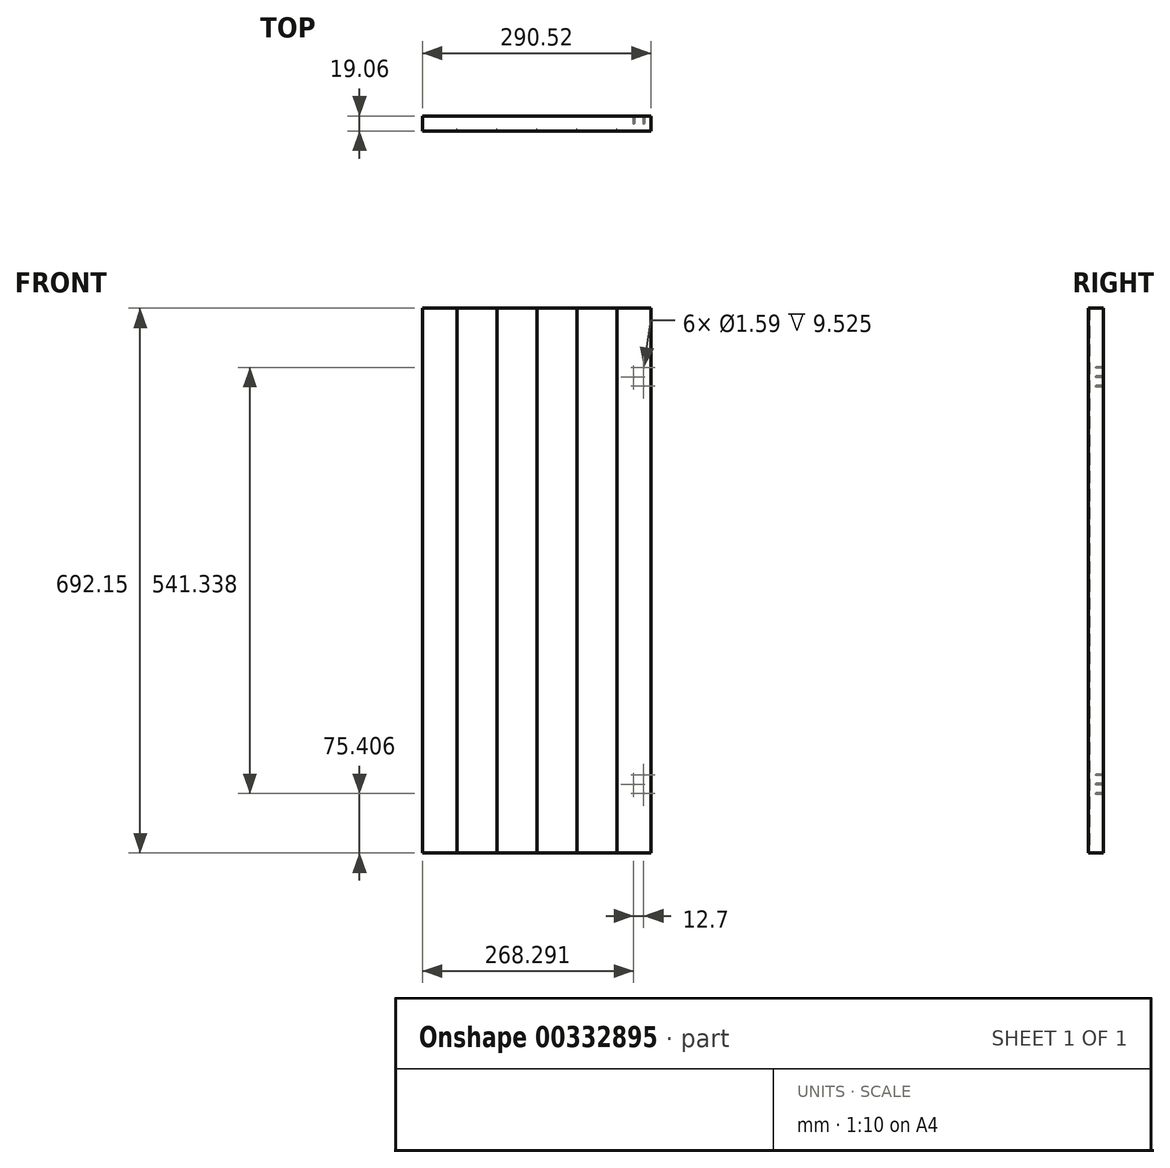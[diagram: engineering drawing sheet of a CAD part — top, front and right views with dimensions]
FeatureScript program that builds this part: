
annotation { "Feature Type Name" : "Feature", "Feature Type Description" : "" }
export const myFeature = defineFeature(function(context is Context, id is Id, definition is map)
    precondition{}
    {
        {
            var Q0;
            Q0=qCreatedBy(makeId("Top.planeOp"),FACE);
            var sketch = newSketch(context, id + "F0", { "sketchPlane" : qUnion([Q0])});
            skLineSegment(sketch, "E0.bottom", {"start": v(508, -9.53) * mm, "end": v(458.22, -9.53) * mm});
            skLineSegment(sketch, "E0.top", {"start": v(508, 9.53) * mm, "end": v(-508, 9.53) * mm});
            skLineSegment(sketch, "E0.left", {"start": v(508, 9.53) * mm, "end": v(508, -9.53) * mm});
            skLineSegment(sketch, "E0.right", {"start": v(-508, 9.53) * mm, "end": v(-508, -9.53) * mm});
            skPoint(sketch, "E0.middle", {"position": v(0, 0) * mm});
            skArc(sketch, "E1", {"start": v(-509.02, -9.53) * mm, "mid": v(-508.3, -9.23) * mm, "end": v(-508, -8.5) * mm});
            skArc(sketch, "E2", {"start": v(-508, -8.5) * mm, "mid": v(-507.7, -9.23) * mm, "end": v(-506.98, -9.52) * mm});
            skArc(sketch, "E3.1.0.0", {"start": v(-458.22, -9.53) * mm, "mid": v(-457.5, -9.23) * mm, "end": v(-457.2, -8.5) * mm});
            skArc(sketch, "E3.1.0.1", {"start": v(-457.2, -8.5) * mm, "mid": v(-456.9, -9.23) * mm, "end": v(-456.18, -9.52) * mm});
            skArc(sketch, "E3.2.0.0", {"start": v(-407.42, -9.53) * mm, "mid": v(-406.7, -9.23) * mm, "end": v(-406.4, -8.5) * mm});
            skArc(sketch, "E3.2.0.1", {"start": v(-406.4, -8.5) * mm, "mid": v(-406.1, -9.23) * mm, "end": v(-405.38, -9.52) * mm});
            skArc(sketch, "E3.3.0.0", {"start": v(-356.62, -9.53) * mm, "mid": v(-355.9, -9.23) * mm, "end": v(-355.6, -8.5) * mm});
            skArc(sketch, "E3.3.0.1", {"start": v(-355.6, -8.5) * mm, "mid": v(-355.3, -9.23) * mm, "end": v(-354.58, -9.52) * mm});
            skArc(sketch, "E3.4.0.0", {"start": v(-305.82, -9.53) * mm, "mid": v(-305.1, -9.23) * mm, "end": v(-304.8, -8.5) * mm});
            skArc(sketch, "E3.4.0.1", {"start": v(-304.8, -8.5) * mm, "mid": v(-304.5, -9.23) * mm, "end": v(-303.78, -9.52) * mm});
            skArc(sketch, "E3.5.0.0", {"start": v(-255.02, -9.53) * mm, "mid": v(-254.3, -9.23) * mm, "end": v(-254, -8.5) * mm});
            skArc(sketch, "E3.5.0.1", {"start": v(-254, -8.5) * mm, "mid": v(-253.7, -9.23) * mm, "end": v(-252.98, -9.52) * mm});
            skArc(sketch, "E3.6.0.0", {"start": v(-204.22, -9.53) * mm, "mid": v(-203.5, -9.23) * mm, "end": v(-203.2, -8.5) * mm});
            skArc(sketch, "E3.6.0.1", {"start": v(-203.2, -8.5) * mm, "mid": v(-202.9, -9.23) * mm, "end": v(-202.18, -9.52) * mm});
            skArc(sketch, "E3.7.0.0", {"start": v(-153.42, -9.53) * mm, "mid": v(-152.7, -9.23) * mm, "end": v(-152.4, -8.5) * mm});
            skArc(sketch, "E3.7.0.1", {"start": v(-152.4, -8.5) * mm, "mid": v(-152.1, -9.23) * mm, "end": v(-151.38, -9.52) * mm});
            skArc(sketch, "E3.8.0.0", {"start": v(-102.62, -9.53) * mm, "mid": v(-101.9, -9.23) * mm, "end": v(-101.6, -8.5) * mm});
            skArc(sketch, "E3.8.0.1", {"start": v(-101.6, -8.5) * mm, "mid": v(-101.3, -9.23) * mm, "end": v(-100.58, -9.52) * mm});
            skArc(sketch, "E3.9.0.0", {"start": v(-51.82, -9.53) * mm, "mid": v(-51.1, -9.23) * mm, "end": v(-50.8, -8.5) * mm});
            skArc(sketch, "E3.9.0.1", {"start": v(-50.8, -8.5) * mm, "mid": v(-50.5, -9.23) * mm, "end": v(-49.78, -9.52) * mm});
            skArc(sketch, "E3.10.0.0", {"start": v(-1.02, -9.53) * mm, "mid": v(-0.3, -9.23) * mm, "end": v(0, -8.5) * mm});
            skArc(sketch, "E3.10.0.1", {"start": v(0, -8.5) * mm, "mid": v(0.3, -9.23) * mm, "end": v(1.02, -9.52) * mm});
            skArc(sketch, "E3.11.0.0", {"start": v(49.78, -9.53) * mm, "mid": v(50.5, -9.23) * mm, "end": v(50.8, -8.5) * mm});
            skArc(sketch, "E3.11.0.1", {"start": v(50.8, -8.5) * mm, "mid": v(51.1, -9.23) * mm, "end": v(51.82, -9.52) * mm});
            skArc(sketch, "E3.12.0.0", {"start": v(100.58, -9.53) * mm, "mid": v(101.3, -9.23) * mm, "end": v(101.6, -8.5) * mm});
            skArc(sketch, "E3.12.0.1", {"start": v(101.6, -8.5) * mm, "mid": v(101.9, -9.23) * mm, "end": v(102.62, -9.52) * mm});
            skArc(sketch, "E3.13.0.0", {"start": v(151.38, -9.53) * mm, "mid": v(152.1, -9.23) * mm, "end": v(152.4, -8.5) * mm});
            skArc(sketch, "E3.13.0.1", {"start": v(152.4, -8.5) * mm, "mid": v(152.7, -9.23) * mm, "end": v(153.42, -9.52) * mm});
            skArc(sketch, "E3.14.0.0", {"start": v(202.18, -9.53) * mm, "mid": v(202.9, -9.23) * mm, "end": v(203.2, -8.5) * mm});
            skArc(sketch, "E3.14.0.1", {"start": v(203.2, -8.5) * mm, "mid": v(203.5, -9.23) * mm, "end": v(204.22, -9.52) * mm});
            skArc(sketch, "E3.15.0.0", {"start": v(252.98, -9.53) * mm, "mid": v(253.7, -9.23) * mm, "end": v(254, -8.5) * mm});
            skArc(sketch, "E3.15.0.1", {"start": v(254, -8.5) * mm, "mid": v(254.3, -9.23) * mm, "end": v(255.02, -9.52) * mm});
            skArc(sketch, "E3.16.0.0", {"start": v(303.78, -9.53) * mm, "mid": v(304.5, -9.23) * mm, "end": v(304.8, -8.5) * mm});
            skArc(sketch, "E3.16.0.1", {"start": v(304.8, -8.5) * mm, "mid": v(305.1, -9.23) * mm, "end": v(305.82, -9.52) * mm});
            skArc(sketch, "E3.17.0.0", {"start": v(354.58, -9.53) * mm, "mid": v(355.3, -9.23) * mm, "end": v(355.6, -8.5) * mm});
            skArc(sketch, "E3.17.0.1", {"start": v(355.6, -8.5) * mm, "mid": v(355.9, -9.23) * mm, "end": v(356.62, -9.52) * mm});
            skArc(sketch, "E3.18.0.0", {"start": v(405.38, -9.53) * mm, "mid": v(406.1, -9.23) * mm, "end": v(406.4, -8.5) * mm});
            skArc(sketch, "E3.18.0.1", {"start": v(406.4, -8.5) * mm, "mid": v(406.7, -9.23) * mm, "end": v(407.42, -9.52) * mm});
            skArc(sketch, "E3.19.0.0", {"start": v(456.18, -9.53) * mm, "mid": v(456.9, -9.23) * mm, "end": v(457.2, -8.5) * mm});
            skArc(sketch, "E3.19.0.1", {"start": v(457.2, -8.5) * mm, "mid": v(457.5, -9.23) * mm, "end": v(458.22, -9.52) * mm});
            skLineSegment(sketch, "E3.direction1", {"start": v(-506.98, -9.53) * mm, "end": v(-458.22, -9.53) * mm, "construction": true});
            skLineSegment(sketch, "E4.trimOffspring", {"start": v(-458.22, -9.53) * mm, "end": v(-508, -9.53) * mm});
            skLineSegment(sketch, "E5.trimOffspring", {"start": v(-407.42, -9.53) * mm, "end": v(-456.18, -9.53) * mm});
            skLineSegment(sketch, "E6.trimOffspring", {"start": v(-356.62, -9.53) * mm, "end": v(-405.38, -9.53) * mm});
            skLineSegment(sketch, "E7.trimOffspring", {"start": v(-305.82, -9.53) * mm, "end": v(-354.58, -9.53) * mm});
            skLineSegment(sketch, "E8.trimOffspring", {"start": v(-255.02, -9.53) * mm, "end": v(-303.78, -9.53) * mm});
            skLineSegment(sketch, "E9.trimOffspring", {"start": v(-204.22, -9.53) * mm, "end": v(-252.98, -9.53) * mm});
            skLineSegment(sketch, "E10.trimOffspring", {"start": v(-153.42, -9.53) * mm, "end": v(-202.18, -9.53) * mm});
            skLineSegment(sketch, "E11.trimOffspring", {"start": v(-102.62, -9.53) * mm, "end": v(-151.38, -9.53) * mm});
            skLineSegment(sketch, "E12.trimOffspring", {"start": v(-51.82, -9.53) * mm, "end": v(-100.58, -9.53) * mm});
            skLineSegment(sketch, "E13.trimOffspring", {"start": v(-1.02, -9.53) * mm, "end": v(-49.78, -9.53) * mm});
            skLineSegment(sketch, "E14.trimOffspring", {"start": v(49.78, -9.53) * mm, "end": v(1.02, -9.53) * mm});
            skLineSegment(sketch, "E15.trimOffspring", {"start": v(100.58, -9.53) * mm, "end": v(51.82, -9.53) * mm});
            skLineSegment(sketch, "E16.trimOffspring", {"start": v(151.38, -9.53) * mm, "end": v(102.62, -9.53) * mm});
            skLineSegment(sketch, "E17.trimOffspring", {"start": v(202.18, -9.53) * mm, "end": v(153.42, -9.53) * mm});
            skLineSegment(sketch, "E18.trimOffspring", {"start": v(252.98, -9.53) * mm, "end": v(204.22, -9.53) * mm});
            skLineSegment(sketch, "E19.trimOffspring", {"start": v(303.78, -9.53) * mm, "end": v(255.02, -9.53) * mm});
            skLineSegment(sketch, "E20.trimOffspring", {"start": v(354.58, -9.53) * mm, "end": v(305.82, -9.53) * mm});
            skLineSegment(sketch, "E21.trimOffspring", {"start": v(405.38, -9.53) * mm, "end": v(356.62, -9.53) * mm});
            skLineSegment(sketch, "E22.trimOffspring", {"start": v(456.18, -9.53) * mm, "end": v(407.42, -9.53) * mm});
            skSolve(sketch);
        }
        {
            var Q0;
            Q0=qSketchRegion(id+"F0",true);
            extrude(context, id + "F1", {"entities" : qUnion([Q0]), "depth" : 692.15 * mm});
        }
        {
            var Q0;
            Q0=qCreatedBy(makeId("Top.planeOp"),FACE);
            var sketch = newSketch(context, id + "F2", { "sketchPlane" : qUnion([Q0])});
            skLineSegment(sketch, "E23.bottom", {"start": v(145.26, -89.59) * mm, "end": v(526.26, -89.59) * mm});
            skLineSegment(sketch, "E23.top", {"start": v(145.26, 47.64) * mm, "end": v(526.26, 47.64) * mm});
            skLineSegment(sketch, "E23.left", {"start": v(145.26, -89.59) * mm, "end": v(145.26, 47.64) * mm});
            skLineSegment(sketch, "E23.right", {"start": v(526.26, -89.59) * mm, "end": v(526.26, 47.64) * mm});
            skLineSegment(sketch, "E24.bottom", {"start": v(-145.26, -137.09) * mm, "end": v(-526.26, -137.09) * mm});
            skLineSegment(sketch, "E24.top", {"start": v(-145.26, 58.2) * mm, "end": v(-526.26, 58.2) * mm});
            skLineSegment(sketch, "E24.left", {"start": v(-145.26, -137.09) * mm, "end": v(-145.26, 58.2) * mm});
            skLineSegment(sketch, "E24.right", {"start": v(-526.26, -137.09) * mm, "end": v(-526.26, 58.2) * mm});
            skSolve(sketch);
        }
        {
            var Q0;
            Q0=qSketchRegion(id+"F2",true);
            extrude(context, id + "F3", {"entities" : qUnion([Q0]), "operationType" : NewBodyOperationType.REMOVE, "depth" : 1143 * mm});
        }
        {
            var Q0;
            Q0=qCreatedBy(makeId("Front.planeOp"),FACE);
            var sketch = newSketch(context, id + "F4", { "sketchPlane" : qUnion([Q0])});
            skLineSegment(sketch, "E25.bottom", {"start": v(123.03, 0) * mm, "end": v(135.73, 0) * mm, "construction": true});
            skLineSegment(sketch, "E25.top", {"start": v(135.73, 692.15) * mm, "end": v(168.27, 692.15) * mm, "construction": true});
            skLineSegment(sketch, "E25.left", {"start": v(123.03, 0) * mm, "end": v(123.03, 616.74) * mm, "construction": true});
            skLineSegment(sketch, "E25.right", {"start": v(135.73, 0) * mm, "end": v(135.73, 692.15) * mm, "construction": true});
            skLineSegment(sketch, "E26", {"start": v(123.03, 604.84) * mm, "end": v(122.24, 604.84) * mm, "construction": true});
            skLineSegment(sketch, "E27", {"start": v(123.03, 87.31) * mm, "end": v(-344.18, 87.31) * mm, "construction": true});
            skLineSegment(sketch, "E28", {"start": v(135.73, 616.74) * mm, "end": v(123.03, 616.74) * mm, "construction": true});
            skLineSegment(sketch, "E29", {"start": v(123.03, 592.93) * mm, "end": v(135.73, 592.93) * mm, "construction": true});
            skLineSegment(sketch, "E30", {"start": v(-420, 75.4) * mm, "end": v(135.73, 75.4) * mm, "construction": true});
            skLineSegment(sketch, "E31", {"start": v(135.73, 99.22) * mm, "end": v(-422.85, 99.22) * mm, "construction": true});
            skCircle(sketch, "E32", {"center": v(135.73, 616.74) * mm, "radius": 0.8 * mm});
            skCircle(sketch, "E33", {"center": v(123.03, 604.84) * mm, "radius": 0.8 * mm});
            skCircle(sketch, "E34", {"center": v(135.73, 592.93) * mm, "radius": 0.8 * mm});
            skCircle(sketch, "E35", {"center": v(135.73, 99.22) * mm, "radius": 0.8 * mm});
            skCircle(sketch, "E36", {"center": v(123.03, 87.31) * mm, "radius": 0.8 * mm});
            skCircle(sketch, "E37", {"center": v(135.73, 75.4) * mm, "radius": 0.8 * mm});
            skSolve(sketch);
        }
        {
            var Q0;
            Q0=qSketchRegion(id+"F4",true);
            extrude(context, id + "F5", {"entities" : qUnion([Q0]), "operationType" : NewBodyOperationType.REMOVE, "oppositeDirection" : true, "depth" : 25.4 * mm});
        }
    });
